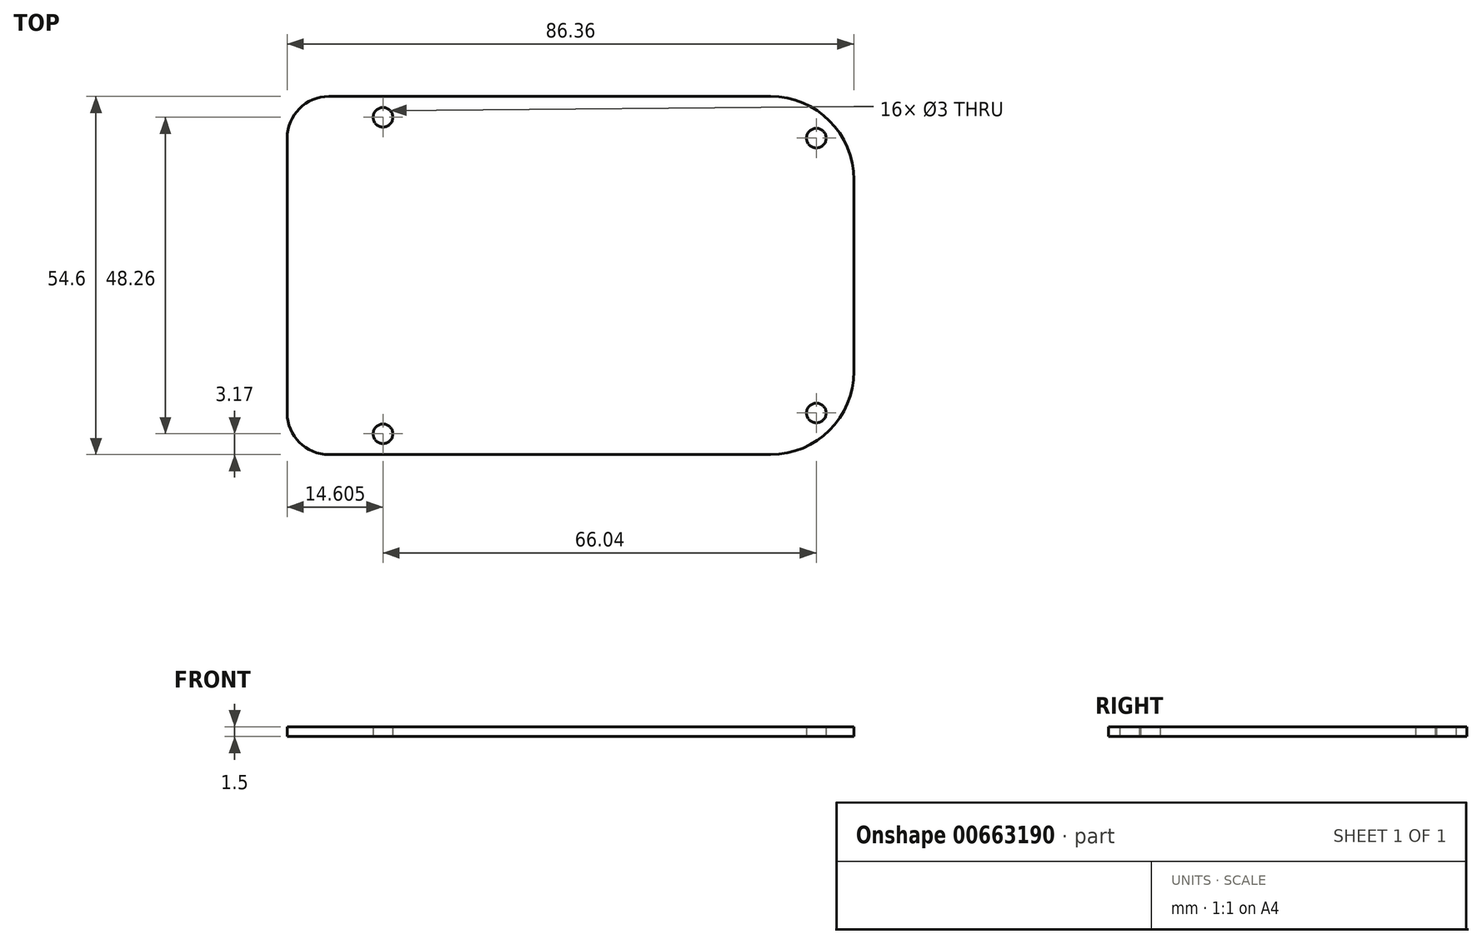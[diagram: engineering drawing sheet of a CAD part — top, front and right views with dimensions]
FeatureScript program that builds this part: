
annotation { "Feature Type Name" : "Feature", "Feature Type Description" : "" }
export const myFeature = defineFeature(function(context is Context, id is Id, definition is map)
    precondition{}
    {
        {
            var Q0;
            Q0=qCreatedBy(makeId("Top.planeOp"),FACE);
            var sketch = newSketch(context, id + "F0", { "sketchPlane" : qUnion([Q0])});
            skLineSegment(sketch, "E0.bottom", {"start": v(-36.83, 27.3) * mm, "end": v(30.48, 27.3) * mm});
            skLineSegment(sketch, "E0.top", {"start": v(-36.83, -27.3) * mm, "end": v(30.48, -27.3) * mm});
            skLineSegment(sketch, "E0.left", {"start": v(-43.18, 20.95) * mm, "end": v(-43.18, -20.95) * mm});
            skLineSegment(sketch, "E0.right", {"start": v(43.18, 14.6) * mm, "end": v(43.18, -14.6) * mm});
            skPoint(sketch, "E1.visualSharp", {"position": v(43.18, 27.3) * mm});
            skArc(sketch, "E1.filletArc", {"start": v(43.18, 14.6) * mm, "mid": v(39.46, 23.59) * mm, "end": v(30.48, 27.3) * mm});
            skPoint(sketch, "E2.visualSharp", {"position": v(43.18, -27.3) * mm});
            skArc(sketch, "E2.filletArc", {"start": v(30.48, -27.3) * mm, "mid": v(39.46, -23.59) * mm, "end": v(43.18, -14.6) * mm});
            skPoint(sketch, "E3.visualSharp", {"position": v(-43.18, 27.3) * mm});
            skArc(sketch, "E3.filletArc", {"start": v(-36.83, 27.3) * mm, "mid": v(-41.32, 25.45) * mm, "end": v(-43.18, 20.95) * mm});
            skPoint(sketch, "E4.visualSharp", {"position": v(-43.18, -27.3) * mm});
            skArc(sketch, "E4.filletArc", {"start": v(-43.18, -20.95) * mm, "mid": v(-41.32, -25.45) * mm, "end": v(-36.83, -27.3) * mm});
            skCircle(sketch, "E5", {"center": v(-28.58, 24.13) * mm, "radius": 1.5 * mm});
            skCircle(sketch, "E6.MirrorC", {"center": v(-28.58, -24.13) * mm, "radius": 1.5 * mm});
            skCircle(sketch, "E7", {"center": v(37.46, -20.95) * mm, "radius": 1.5 * mm});
            skCircle(sketch, "E8.MirrorC", {"center": v(37.46, 20.95) * mm, "radius": 1.5 * mm});
            skSolve(sketch);
        }
        {
            var Q0;
            Q0 = qSketchRegion(id + "F0", true);
            extrude(context, id + "F1", {"entities" : qUnion([Q0]), "depth" : 1.5 * mm, "offsetDistance" : 25 * mm});
        }
    });
